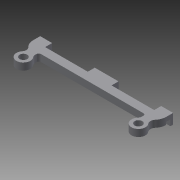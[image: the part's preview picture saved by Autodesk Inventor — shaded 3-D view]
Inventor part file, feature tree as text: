
AUTODESK INVENTOR PART (.ipt)
format: ipt  version: 2015 (Build 190159000, 159)  size: 257,536 bytes
history: native  units: in
note: dims shown in document units (in); Inventor stores cm internally (conversion verified against a paired STEP export)
features: extrude x7, pattern_linear x6, sketch x6, projected_geometry x3, fillet x2
ambient origin geometry x8: Origin, YZ Plane, XZ Plane, XY Plane, X Axis, Y Axis, Z Axis, Center Point
bodies: Solid1 (feature_tree)
feature tree (24):
  extrude  "Extrusion1"  Depth=1.95in
  extrude  "Extrusion2"  Depth=0.2362in
  extrude  "Extrusion3"  Depth=0.1181in TaperAngle=0.0deg
  pattern_linear  "Rectangular Pattern1"  Spacing1=0.1378in  [1 undecoded]
  extrude  "Extrusion4"  Depth=0.1012in
  pattern_linear  "Rectangular Pattern2"  Spacing1=0.0394in  [1 undecoded]
  pattern_linear  "Rectangular Pattern3"  Spacing1=0.0787in  [1 undecoded]
  extrude  "Extrusion5"  Depth=0.1181in TaperAngle=0.0deg
  extrude  "Extrusion6"  Depth=0.045in
  pattern_linear  "Rectangular Pattern4"  Spacing1=0.1181in  [1 undecoded]
  pattern_linear  "Rectangular Pattern5"  Spacing1=0.9544in  [1 undecoded]
  pattern_linear  "Rectangular Pattern6"  Spacing1=0.0787in  [1 undecoded]
  extrude  "Extrusion7"  Depth=0.0787in
  fillet  "Fillet2"  Radius=0.025in
  fillet  "Fillet3"  Radius=0.025in
  sketch  "Sketch1"  dims[d0=0.1299in d2=1.95in]
  sketch  "Sketch2"  dims[d3=0.1299in d4=0.2362in]
  sketch  "Sketch3"  dims[d11=0.2362in d12=0.1181in d13=0.0in]
  sketch  "Sketch4"  dims[d14=0.2417in]
  sketch  "Sketch7"  dims[d15=0.0866in]
  projected_geometry  "Projected Loop1"
  sketch  "Sketch9"  dims[d16=0.1378in d17=0.1378in d18=0.0866in d19=0.0394in d20=0.0787in d21=0.1181in d22=0.0in d23=0.045in d24=0.1181in d25=0.0in d26=0.9544in d27=0.0787in d28=0.0787in d29=0.025in d30=0.025in d31=0.0956in d32=0.7874in d34=0.925in d35=0.1181in d36=0.0in d37=0.7874in d39=0.2in d40=0.7874in d42=0.925in d43=0.1181in d44=0.0in d46=0.0472in d47=0.0in d48=0.7874in d50=0.925in d51=0.7874in d53=1.125in d54=0.7874in d56=2.05in d77=0.0394in d78=0.0in d86=0.0787in d87=0.0787in d96=0.1012in]
  projected_geometry  "Projected Loop5"
  projected_geometry  "Projected Loop6"
note: 6 required parameter values undecoded (feature->parameter linkage not recoverable at this tier; creation-order binding heuristic only, values carry confidence <= 0.55)
